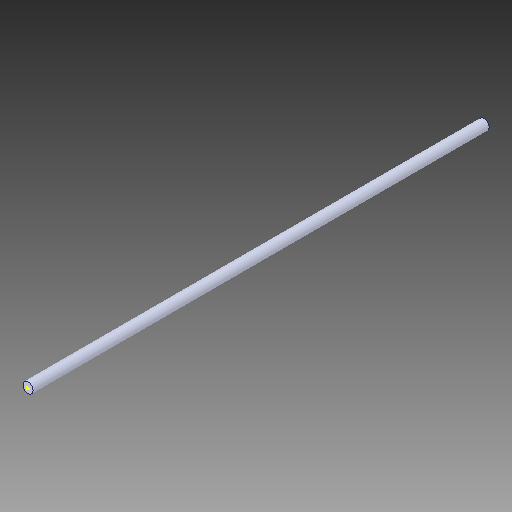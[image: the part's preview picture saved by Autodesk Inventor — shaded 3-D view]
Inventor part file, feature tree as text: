
AUTODESK INVENTOR PART (.ipt)
format: ipt  version: 2018 (Build 220112000, 112)  size: 78,848 bytes
history: native  units: in
note: dims shown in document units (in); Inventor stores cm internally (conversion verified against a paired STEP export)
features: sketch x1, other x1
ambient origin geometry x8: Origin, YZ Plane, XZ Plane, XY Plane, X Axis, Y Axis, Z Axis, Center Point
bodies: Solid1 (feature_tree)
feature tree (2):
  sketch  "Sketch1"
  other  "Boss-Extrude1"
